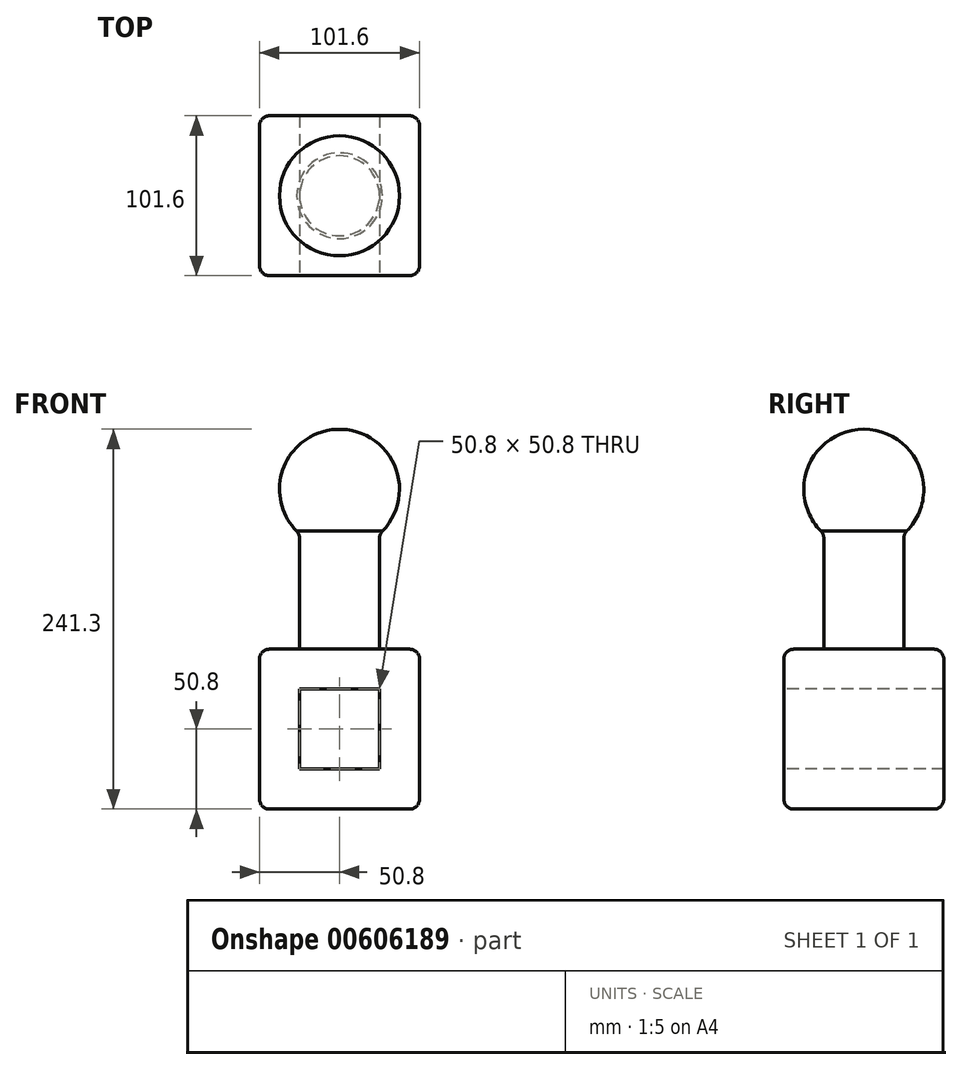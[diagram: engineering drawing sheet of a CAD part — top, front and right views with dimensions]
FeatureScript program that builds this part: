
annotation { "Feature Type Name" : "Feature", "Feature Type Description" : "" }
export const myFeature = defineFeature(function(context is Context, id is Id, definition is map)
    precondition{}
    {
        {
            var Q0;
            Q0=qCreatedBy(makeId("Top.planeOp"),FACE);
            var sketch = newSketch(context, id + "F0", { "sketchPlane" : qUnion([Q0])});
            skLineSegment(sketch, "E0.bottom", {"start": v(50.8, 50.8) * mm, "end": v(-50.8, 50.8) * mm});
            skLineSegment(sketch, "E0.top", {"start": v(50.8, -50.8) * mm, "end": v(-50.8, -50.8) * mm});
            skLineSegment(sketch, "E0.left", {"start": v(50.8, 50.8) * mm, "end": v(50.8, -50.8) * mm});
            skLineSegment(sketch, "E0.right", {"start": v(-50.8, 50.8) * mm, "end": v(-50.8, -50.8) * mm});
            skPoint(sketch, "E0.middle", {"position": v(0, 0) * mm});
            skSolve(sketch);
        }
        {
            var Q0;
            Q0 = qSketchRegion(id + "F0", true);
            extrude(context, id + "F1", {"entities" : qUnion([Q0]), "depth" : 101.6 * mm, "offsetDistance" : 25.4 * mm});
        }
        {
            var Q0;
            Q0=makeQuery(id+"F1.opExtrude","CAP_FACE",FACE,{"disambiguationData":[OSD([sQuery(id+"F0.wireOp",EDGE,"E0.bottom"),sQuery(id+"F0.wireOp",EDGE,"E0.top"),sQuery(id+"F0.wireOp",EDGE,"E0.left"),sQuery(id+"F0.wireOp",EDGE,"E0.right")])],"isStart":false});
            var sketch = newSketch(context, id + "F2", { "sketchPlane" : qUnion([Q0])});
            skCircle(sketch, "E1", {"center": v(0, 0) * mm, "radius": 25.4 * mm});
            skSolve(sketch);
        }
        {
            var Q0;
            Q0=makeQuery(id+"F2.imprint","IMPRINT",FACE,{"disambiguationData":[TD([[makeQuery(id+"F2.imprint","IMPRINT",EDGE,{"derivedFrom":sQuery(id+"F2.wireOp",EDGE,"E1")}),1.0]])]});
            extrude(context, id + "F3", {"entities" : qUnion([Q0]), "operationType" : NewBodyOperationType.ADD, "depth" : 101.6 * mm, "offsetDistance" : 25.4 * mm});
        }
        {
            var Q0;
            Q0=makeQuery(id+"F3.opExtrude","CAP_FACE",FACE,{"disambiguationData":[OSD([sQuery(id+"F2.wireOp",EDGE,"E1")])],"isStart":false});
            var sketch = newSketch(context, id + "F4", { "sketchPlane" : qUnion([Q0])});
            skArc(sketch, "E2", {"start": v(0, -38.1) * mm, "mid": v(38.1, 0) * mm, "end": v(0, 38.1) * mm});
            skLineSegment(sketch, "E3", {"start": v(0, 38.1) * mm, "end": v(0, 0) * mm});
            skLineSegment(sketch, "E4", {"start": v(0, -38.1) * mm, "end": v(0, 0) * mm});
            skSolve(sketch);
        }
        {
            var Q0;
            {var subQ0=sQuery(id+"F4.wireOp",EDGE,"E4");var subQ1=sQuery(id+"F4.wireOp",EDGE,"E3");var subQ2=makeQuery(id+"F4.imprint","INTERSECT",VERTEX,{"derivedFrom":[subQ1,subQ0]});Q0=makeQuery(id+"F4.imprint","IMPRINT",FACE,{"disambiguationData":[TD([[makeQuery(id+"F4.imprint","IMPRINT",EDGE,{"disambiguationData":[TD([[subQ2,1.0]])],"derivedFrom":subQ1}),1.0]])]});}
            var Q1;
            {var subQ0=sQuery(id+"F4.wireOp",EDGE,"E2");Q1=makeQuery(id+"F4.imprint","IMPRINT",FACE,{"disambiguationData":[TD([[makeQuery(id+"F4.imprint","IMPRINT",EDGE,{"derivedFrom":subQ0}),1.0]])]});}
            var Q2;
            Q2=sQuery(id+"F4.wireOp",EDGE,"E4");
            revolve(context, id + "F5", {"operationType" : NewBodyOperationType.ADD, "entities" : qUnion([Q0, Q1]), "axis" : qUnion([Q2]), "revolveType" : RevolveType.FULL});
        }
        {
            var Q0;
            Q0=makeQuery(id+"F1.opExtrude","SWEPT_FACE",FACE,{"disambiguationData":[OSD([sQuery(id+"F0.wireOp",EDGE,"E0.top")])]});
            var sketch = newSketch(context, id + "F6", { "sketchPlane" : qUnion([Q0])});
            skPoint(sketch, "E5.firstSnap0", {"position": v(50.8, 50.8) * mm});
            skLineSegment(sketch, "E6.bottom", {"start": v(25.4, 25.4) * mm, "end": v(-25.4, 25.4) * mm});
            skLineSegment(sketch, "E6.top", {"start": v(25.4, 76.2) * mm, "end": v(-25.4, 76.2) * mm});
            skLineSegment(sketch, "E6.left", {"start": v(25.4, 25.4) * mm, "end": v(25.4, 76.2) * mm});
            skLineSegment(sketch, "E6.right", {"start": v(-25.4, 25.4) * mm, "end": v(-25.4, 76.2) * mm});
            skPoint(sketch, "E6.middle", {"position": v(0, 50.8) * mm});
            skSolve(sketch);
        }
        {
            var Q0;
            Q0=makeQuery(id+"F6.imprint","IMPRINT",FACE,{"disambiguationData":[TD([[makeQuery(id+"F6.imprint","IMPRINT",EDGE,{"derivedFrom":sQuery(id+"F6.wireOp",EDGE,"E6.bottom")}),-1.0]])]});
            extrude(context, id + "F7", {"entities" : qUnion([Q0]), "operationType" : NewBodyOperationType.REMOVE, "oppositeDirection" : true, "depth" : 101.6 * mm, "offsetDistance" : 25.4 * mm});
        }
        {
            var Q0;
            Q0=makeQuery(id+"F1.opExtrude","SWEPT_EDGE",EDGE,{"disambiguationData":[OSD([sQuery(id+"F0.wireOp",EDGE,"E0.bottom"),sQuery(id+"F0.wireOp",EDGE,"E0.left")])]});
            var Q1;
            Q1=makeQuery(id+"F1.opExtrude","SWEPT_EDGE",EDGE,{"disambiguationData":[OSD([sQuery(id+"F0.wireOp",EDGE,"E0.bottom"),sQuery(id+"F0.wireOp",EDGE,"E0.right")])]});
            var Q2;
            Q2=makeQuery(id+"F1.opExtrude","SWEPT_EDGE",EDGE,{"disambiguationData":[OSD([sQuery(id+"F0.wireOp",EDGE,"E0.top"),sQuery(id+"F0.wireOp",EDGE,"E0.left")])]});
            var Q3;
            Q3=makeQuery(id+"F1.opExtrude","SWEPT_EDGE",EDGE,{"disambiguationData":[OSD([sQuery(id+"F0.wireOp",EDGE,"E0.top"),sQuery(id+"F0.wireOp",EDGE,"E0.right")])]});
            var Q4;
            Q4=makeQuery(id+"F1.opExtrude","CAP_EDGE",EDGE,{"disambiguationData":[OSD([sQuery(id+"F0.wireOp",EDGE,"E0.right")])],"isStart":true});
            var Q5;
            Q5=makeQuery(id+"F1.opExtrude","CAP_EDGE",EDGE,{"disambiguationData":[OSD([sQuery(id+"F0.wireOp",EDGE,"E0.right")])],"isStart":false});
            var Q6;
            Q6=makeQuery(id+"F1.opExtrude","CAP_EDGE",EDGE,{"disambiguationData":[OSD([sQuery(id+"F0.wireOp",EDGE,"E0.bottom")])],"isStart":true});
            var Q7;
            Q7=makeQuery(id+"F1.opExtrude","CAP_EDGE",EDGE,{"disambiguationData":[OSD([sQuery(id+"F0.wireOp",EDGE,"E0.bottom")])],"isStart":false});
            var Q8;
            Q8=makeQuery(id+"F1.opExtrude","CAP_EDGE",EDGE,{"disambiguationData":[OSD([sQuery(id+"F0.wireOp",EDGE,"E0.top")])],"isStart":false});
            var Q9;
            Q9=makeQuery(id+"F1.opExtrude","CAP_EDGE",EDGE,{"disambiguationData":[OSD([sQuery(id+"F0.wireOp",EDGE,"E0.top")])],"isStart":true});
            var Q10;
            Q10=makeQuery(id+"F1.opExtrude","CAP_EDGE",EDGE,{"disambiguationData":[OSD([sQuery(id+"F0.wireOp",EDGE,"E0.left")])],"isStart":false});
            var Q11;
            Q11=makeQuery(id+"F1.opExtrude","CAP_EDGE",EDGE,{"disambiguationData":[OSD([sQuery(id+"F0.wireOp",EDGE,"E0.left")])],"isStart":true});
            var Q12;
            Q12=makeQuery(id+"F3.opExtrude","CAP_EDGE",EDGE,{"disambiguationData":[OSD([sQuery(id+"F2.wireOp",EDGE,"E1")])],"isStart":true});
            var Q13;
            Q13=makeQuery(id+"F5.boolean.opBoolean","INTERSECT",EDGE,{"derivedFrom":[makeQuery(id+"F3.opExtrude","SWEPT_FACE",FACE,{"disambiguationData":[OSD([sQuery(id+"F2.wireOp",EDGE,"E1")])]}),makeQuery(id+"F5.opRevolve","SWEPT_FACE",FACE,{"disambiguationData":[OSD([sQuery(id+"F4.wireOp",EDGE,"E2")])]})]});
            fillet(context, id + "F8", {"entities" : qUnion([Q0, Q1, Q2, Q3, Q4, Q5, Q6, Q7, Q8, Q9, Q10, Q11, Q12, Q13]), "radius" : 6.35 * mm, "tangentPropagation" : true, "allowEdgeOverflow" : false});
        }
    });
